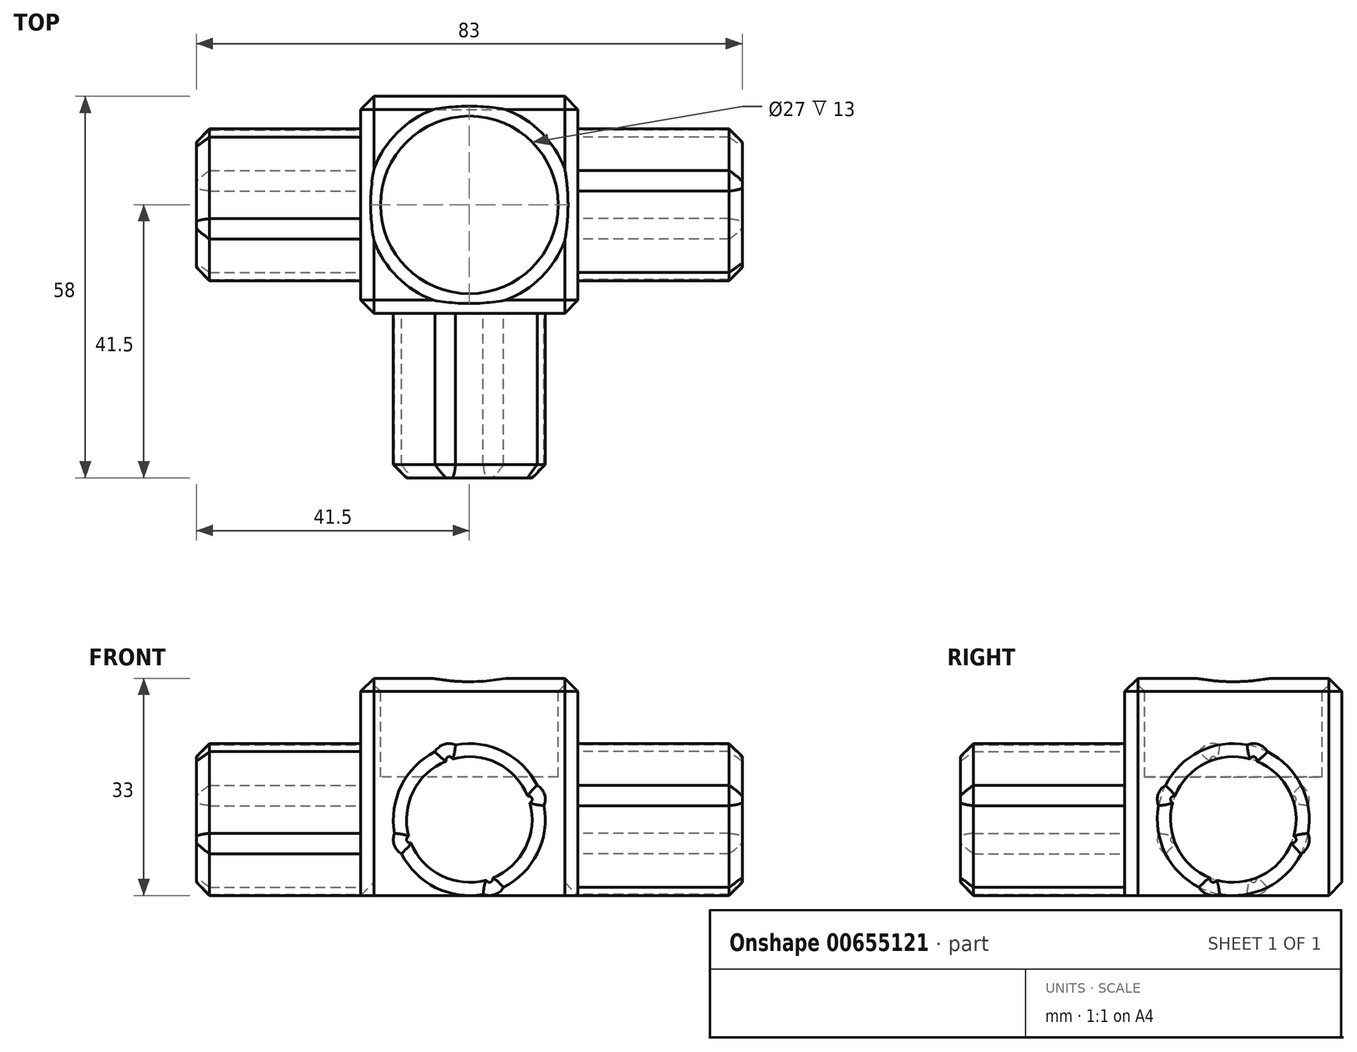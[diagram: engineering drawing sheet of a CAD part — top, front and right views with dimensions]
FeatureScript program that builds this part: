
annotation { "Feature Type Name" : "Feature", "Feature Type Description" : "" }
export const myFeature = defineFeature(function(context is Context, id is Id, definition is map)
    precondition{}
    {
        {
            var Q0;
            Q0=qCreatedBy(makeId("Front.planeOp"),FACE);
            var sketch = newSketch(context, id + "F0", { "sketchPlane" : qUnion([Q0])});
            skLineSegment(sketch, "E0.bottom", {"start": v(-16.5, 0) * mm, "end": v(16.5, 0) * mm});
            skLineSegment(sketch, "E0.top", {"start": v(-16.5, 33) * mm, "end": v(16.5, 33) * mm});
            skLineSegment(sketch, "E0.left", {"start": v(-16.5, 0) * mm, "end": v(-16.5, 33) * mm});
            skLineSegment(sketch, "E0.right", {"start": v(16.5, 0) * mm, "end": v(16.5, 33) * mm});
            skSolve(sketch);
        }
        {
            var Q0;
            Q0=qSketchRegion(id+"F0",true);
            extrude(context, id + "F1", {"entities" : qUnion([Q0]), "depth" : 33 * mm, "offsetDistance" : 25 * mm, "symmetric" : true});
        }
        {
            var Q0;
            Q0=makeQuery(id+"F1.opExtrude","CAP_FACE",FACE,{"disambiguationData":[OSD([sQuery(id+"F0.wireOp",EDGE,"E0.bottom"),sQuery(id+"F0.wireOp",EDGE,"E0.top"),sQuery(id+"F0.wireOp",EDGE,"E0.left"),sQuery(id+"F0.wireOp",EDGE,"E0.right")])],"isStart":false});
            var sketch = newSketch(context, id + "F2", { "sketchPlane" : qUnion([Q0])});
            skArc(sketch, "E1", {"start": v(-10.3, 6.34) * mm, "mid": v(-5.13, 1.2) * mm, "end": v(2.1, 0.2) * mm});
            skArc(sketch, "E2", {"start": v(-11.36, 9.46) * mm, "mid": v(-11.42, 7.7) * mm, "end": v(-10.3, 6.34) * mm});
            skArc(sketch, "E3.1.0", {"start": v(2.1, 0.2) * mm, "mid": v(3.85, 0.13) * mm, "end": v(5.2, 1.24) * mm});
            skArc(sketch, "E3.2.0", {"start": v(11.36, 13.64) * mm, "mid": v(11.42, 15.4) * mm, "end": v(10.3, 16.76) * mm});
            skArc(sketch, "E4.1.3.0", {"start": v(-2.1, 22.9) * mm, "mid": v(-3.85, 22.97) * mm, "end": v(-5.2, 21.86) * mm});
            skArc(sketch, "E5.trimOffspring", {"start": v(-5.2, 21.86) * mm, "mid": v(-10.35, 16.68) * mm, "end": v(-11.36, 9.46) * mm});
            skArc(sketch, "E6.trimOffspring", {"start": v(10.3, 16.76) * mm, "mid": v(5.13, 21.9) * mm, "end": v(-2.1, 22.9) * mm});
            skArc(sketch, "E7.trimOffspring", {"start": v(5.2, 1.24) * mm, "mid": v(10.35, 6.42) * mm, "end": v(11.36, 13.64) * mm});
            skSolve(sketch);
        }
        {
            var Q0;
            Q0=makeQuery(id+"F2.imprint","IMPRINT",FACE,{"disambiguationData":[TD([[makeQuery(id+"F2.imprint","IMPRINT",EDGE,{"derivedFrom":sQuery(id+"F2.wireOp",EDGE,"E1")}),1.0]])]});
            extrude(context, id + "F3", {"entities" : qUnion([Q0]), "operationType" : NewBodyOperationType.ADD, "depth" : 25 * mm, "offsetDistance" : 25 * mm});
        }
        {
            var Q0;
            Q0=makeQuery(id+"F1.opExtrude","SWEPT_FACE",FACE,{"disambiguationData":[OSD([sQuery(id+"F0.wireOp",EDGE,"E0.right")])]});
            var sketch = newSketch(context, id + "F4", { "sketchPlane" : qUnion([Q0])});
            skArc(sketch, "E8", {"start": v(-11.36, 13.64) * mm, "mid": v(-10.35, 6.42) * mm, "end": v(-5.2, 1.24) * mm});
            skArc(sketch, "E9", {"start": v(-10.3, 16.76) * mm, "mid": v(-11.42, 15.4) * mm, "end": v(-11.36, 13.64) * mm});
            skArc(sketch, "E10.1.0", {"start": v(-5.2, 1.24) * mm, "mid": v(-3.85, 0.13) * mm, "end": v(-2.1, 0.2) * mm});
            skArc(sketch, "E10.2.0", {"start": v(10.3, 6.34) * mm, "mid": v(11.42, 7.7) * mm, "end": v(11.36, 9.46) * mm});
            skArc(sketch, "E10.3.0", {"start": v(5.2, 21.86) * mm, "mid": v(3.85, 22.97) * mm, "end": v(2.1, 22.9) * mm});
            skArc(sketch, "E11.trimOffspring", {"start": v(2.1, 22.9) * mm, "mid": v(-5.13, 21.9) * mm, "end": v(-10.3, 16.76) * mm});
            skArc(sketch, "E12.trimOffspring", {"start": v(11.36, 9.46) * mm, "mid": v(10.35, 16.68) * mm, "end": v(5.2, 21.86) * mm});
            skArc(sketch, "E13.trimOffspring", {"start": v(-2.1, 0.2) * mm, "mid": v(5.13, 1.2) * mm, "end": v(10.3, 6.34) * mm});
            skSolve(sketch);
        }
        {
            var Q0;
            Q0=qSketchRegion(id+"F4",true);
            extrude(context, id + "F5", {"entities" : qUnion([Q0]), "operationType" : NewBodyOperationType.ADD, "depth" : 25 * mm, "offsetDistance" : 25 * mm});
        }
        {
            var Q0;
            Q0=makeQuery(id+"F1.opExtrude","SWEPT_FACE",FACE,{"disambiguationData":[OSD([sQuery(id+"F0.wireOp",EDGE,"E0.top")])]});
            var sketch = newSketch(context, id + "F6", { "sketchPlane" : qUnion([Q0])});
            skCircle(sketch, "E14", {"center": v(0, 0) * mm, "radius": 13.5 * mm});
            skSolve(sketch);
        }
        {
            var Q0;
            Q0=makeQuery(id+"F6.imprint","IMPRINT",FACE,{"disambiguationData":[TD([[makeQuery(id+"F6.imprint","IMPRINT",EDGE,{"derivedFrom":sQuery(id+"F6.wireOp",EDGE,"E14")}),1.0]])]});
            extrude(context, id + "F7", {"entities" : qUnion([Q0]), "operationType" : NewBodyOperationType.REMOVE, "oppositeDirection" : true, "depth" : 15 * mm, "offsetDistance" : 25 * mm});
        }
        {
            var Q0;
            Q0=makeQuery(id+"F1.opExtrude","SWEPT_FACE",FACE,{"disambiguationData":[OSD([sQuery(id+"F0.wireOp",EDGE,"E0.left")])]});
            var sketch = newSketch(context, id + "F8", { "sketchPlane" : qUnion([Q0])});
            skArc(sketch, "E15", {"start": v(-11.36, 13.64) * mm, "mid": v(-10.35, 6.42) * mm, "end": v(-5.2, 1.24) * mm});
            skArc(sketch, "E16", {"start": v(-10.3, 16.76) * mm, "mid": v(-11.42, 15.4) * mm, "end": v(-11.36, 13.64) * mm});
            skArc(sketch, "E17.1.0", {"start": v(-5.2, 1.24) * mm, "mid": v(-3.85, 0.13) * mm, "end": v(-2.1, 0.2) * mm});
            skArc(sketch, "E17.2.0", {"start": v(10.3, 6.34) * mm, "mid": v(11.42, 7.7) * mm, "end": v(11.36, 9.46) * mm});
            skArc(sketch, "E17.3.0", {"start": v(5.2, 21.86) * mm, "mid": v(3.85, 22.97) * mm, "end": v(2.1, 22.9) * mm});
            skArc(sketch, "E18.trimOffspring", {"start": v(2.1, 22.9) * mm, "mid": v(-5.13, 21.9) * mm, "end": v(-10.3, 16.76) * mm});
            skArc(sketch, "E19.trimOffspring", {"start": v(11.36, 9.46) * mm, "mid": v(10.35, 16.68) * mm, "end": v(5.2, 21.86) * mm});
            skArc(sketch, "E20.trimOffspring", {"start": v(-2.1, 0.2) * mm, "mid": v(5.13, 1.2) * mm, "end": v(10.3, 6.34) * mm});
            skSolve(sketch);
        }
        {
            var Q0;
            {var subQ7=sQuery(id+"F8.wireOp",EDGE,"E16");Q0=makeQuery(id+"F8.imprint","IMPRINT",FACE,{"disambiguationData":[TD([[makeQuery(id+"F8.imprint","IMPRINT",EDGE,{"derivedFrom":subQ7}),1.0]])]});}
            extrude(context, id + "F9", {"entities" : qUnion([Q0]), "operationType" : NewBodyOperationType.ADD, "depth" : 25 * mm, "offsetDistance" : 25 * mm});
        }
        {
            var Q0;
            Q0=makeQuery(id+"F1.opExtrude","SWEPT_FACE",FACE,{"disambiguationData":[OSD([sQuery(id+"F0.wireOp",EDGE,"E0.top")])]});
            var Q1;
            Q1=makeQuery(id+"F1.opExtrude","CAP_FACE",FACE,{"disambiguationData":[OSD([sQuery(id+"F0.wireOp",EDGE,"E0.bottom"),sQuery(id+"F0.wireOp",EDGE,"E0.top"),sQuery(id+"F0.wireOp",EDGE,"E0.left"),sQuery(id+"F0.wireOp",EDGE,"E0.right")])],"isStart":true});
            var Q2;
            Q2=makeQuery(id+"F1.opExtrude","CAP_EDGE",EDGE,{"disambiguationData":[OSD([sQuery(id+"F0.wireOp",EDGE,"E0.right")])],"isStart":false});
            var Q3;
            Q3=makeQuery(id+"F3.opExtrude","CAP_FACE",FACE,{"disambiguationData":[OSD([sQuery(id+"F2.wireOp",EDGE,"E1"),sQuery(id+"F2.wireOp",EDGE,"E2"),sQuery(id+"F2.wireOp",EDGE,"E3.1.0"),sQuery(id+"F2.wireOp",EDGE,"E3.2.0"),sQuery(id+"F2.wireOp",EDGE,"E4.1.3.0"),sQuery(id+"F2.wireOp",EDGE,"E5.trimOffspring"),sQuery(id+"F2.wireOp",EDGE,"E6.trimOffspring"),sQuery(id+"F2.wireOp",EDGE,"E7.trimOffspring")])],"isStart":false});
            var Q4;
            Q4=makeQuery(id+"F5.opExtrude","CAP_FACE",FACE,{"disambiguationData":[OSD([sQuery(id+"F4.wireOp",EDGE,"E8"),sQuery(id+"F4.wireOp",EDGE,"E9"),sQuery(id+"F4.wireOp",EDGE,"E10.1.0"),sQuery(id+"F4.wireOp",EDGE,"E10.2.0"),sQuery(id+"F4.wireOp",EDGE,"E10.3.0"),sQuery(id+"F4.wireOp",EDGE,"E11.trimOffspring"),sQuery(id+"F4.wireOp",EDGE,"E12.trimOffspring"),sQuery(id+"F4.wireOp",EDGE,"E13.trimOffspring")])],"isStart":false});
            var Q5;
            Q5=makeQuery(id+"F1.opExtrude","CAP_EDGE",EDGE,{"disambiguationData":[OSD([sQuery(id+"F0.wireOp",EDGE,"E0.left")])],"isStart":false});
            var Q6;
            Q6=makeQuery(id+"F9.opExtrude","CAP_FACE",FACE,{"disambiguationData":[OSD([sQuery(id+"F8.wireOp",EDGE,"E15"),sQuery(id+"F8.wireOp",EDGE,"E16"),sQuery(id+"F8.wireOp",EDGE,"E17.1.0"),sQuery(id+"F8.wireOp",EDGE,"E17.2.0"),sQuery(id+"F8.wireOp",EDGE,"E17.3.0"),sQuery(id+"F8.wireOp",EDGE,"E18.trimOffspring"),sQuery(id+"F8.wireOp",EDGE,"E19.trimOffspring"),sQuery(id+"F8.wireOp",EDGE,"E20.trimOffspring")])],"isStart":false});
            chamfer(context, id + "F10", {"entities" : qUnion([Q0, Q1, Q2, Q3, Q4, Q5, Q6]), "width" : 2 * mm, "tangentPropagation" : true});
        }
    });
